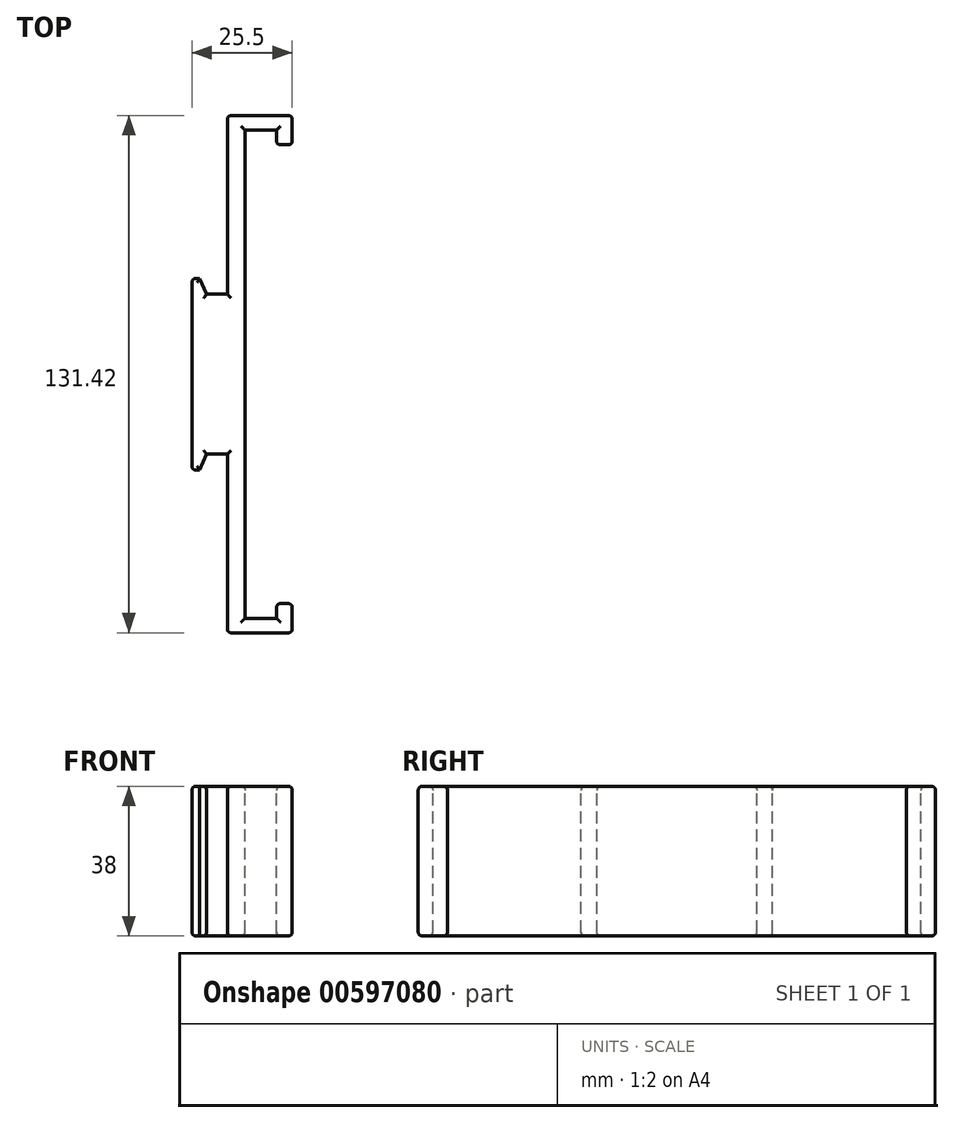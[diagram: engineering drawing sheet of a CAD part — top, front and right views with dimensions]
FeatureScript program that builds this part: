
annotation { "Feature Type Name" : "Feature", "Feature Type Description" : "" }
export const myFeature = defineFeature(function(context is Context, id is Id, definition is map)
    precondition{}
    {
        {
            var Q0;
            Q0=qCreatedBy(makeId("Top.planeOp"),FACE);
            var sketch = newSketch(context, id + "F0", { "sketchPlane" : qUnion([Q0])});
            skLineSegment(sketch, "E0", {"start": v(0, 0) * mm, "end": v(0, 65.71) * mm});
            skLineSegment(sketch, "E1", {"start": v(0, 65.71) * mm, "end": v(12.5, 65.71) * mm});
            skLineSegment(sketch, "E2", {"start": v(12.5, 62) * mm, "end": v(12.5, 58.29) * mm});
            skLineSegment(sketch, "E3", {"start": v(16.5, 58.29) * mm, "end": v(12.5, 58.29) * mm});
            skLineSegment(sketch, "E4", {"start": v(16.5, 58.29) * mm, "end": v(16.5, 62) * mm});
            skPoint(sketch, "E4.endSnap0", {"position": v(12.5, 62) * mm});
            skLineSegment(sketch, "E5", {"start": v(12.5, 62) * mm, "end": v(4.5, 62) * mm});
            skLineSegment(sketch, "E6", {"start": v(4.5, 62) * mm, "end": v(4.5, 0) * mm});
            skLineSegment(sketch, "E7", {"start": v(0, 20.33) * mm, "end": v(-5.29, 20.33) * mm});
            skLineSegment(sketch, "E8", {"start": v(-7, 24.33) * mm, "end": v(-9, 24.33) * mm});
            skLineSegment(sketch, "E9", {"start": v(-9, 24.33) * mm, "end": v(-9, 0) * mm});
            skLineSegment(sketch, "E10", {"start": v(16.5, 62) * mm, "end": v(16.5, 65.71) * mm});
            skLineSegment(sketch, "E11", {"start": v(16.5, 65.71) * mm, "end": v(12.5, 65.71) * mm});
            skLineSegment(sketch, "E12", {"start": v(0, 0) * mm, "end": v(27.16, 0) * mm, "construction": true});
            skLineSegment(sketch, "E13.MirrorCS", {"start": v(0, 0) * mm, "end": v(0, -65.71) * mm});
            skLineSegment(sketch, "E14.MirrorCS", {"start": v(4.5, -62) * mm, "end": v(4.5, 0) * mm});
            skLineSegment(sketch, "E15.MirrorCS", {"start": v(12.5, -62) * mm, "end": v(4.5, -62) * mm});
            skLineSegment(sketch, "E16.MirrorCS", {"start": v(0, -65.71) * mm, "end": v(12.5, -65.71) * mm});
            skLineSegment(sketch, "E17.MirrorCS", {"start": v(12.5, -62) * mm, "end": v(12.5, -58.29) * mm});
            skLineSegment(sketch, "E18.MirrorCS", {"start": v(16.5, -62) * mm, "end": v(16.5, -65.71) * mm});
            skLineSegment(sketch, "E19.MirrorCS", {"start": v(16.5, -58.29) * mm, "end": v(16.5, -62) * mm});
            skLineSegment(sketch, "E20.MirrorCS", {"start": v(16.5, -65.71) * mm, "end": v(12.5, -65.71) * mm});
            skLineSegment(sketch, "E21.MirrorCS", {"start": v(16.5, -58.29) * mm, "end": v(12.5, -58.29) * mm});
            skLineSegment(sketch, "E22.MirrorCS", {"start": v(0, -20.33) * mm, "end": v(-5.29, -20.33) * mm});
            skLineSegment(sketch, "E23.MirrorCS", {"start": v(-7, -24.33) * mm, "end": v(-9, -24.33) * mm});
            skLineSegment(sketch, "E24.MirrorCS", {"start": v(-9, -24.33) * mm, "end": v(-9, 0) * mm});
            skLineSegment(sketch, "E25", {"start": v(-7, 24.33) * mm, "end": v(-5.29, 20.33) * mm});
            skPoint(sketch, "E26.orphan", {"position": v(-7, 20.33) * mm});
            skLineSegment(sketch, "E27.MirrorCS", {"start": v(-7, -24.33) * mm, "end": v(-5.29, -20.33) * mm});
            skPoint(sketch, "E28.orphan", {"position": v(-7, -20.33) * mm});
            skPoint(sketch, "E29.MirrorCS.end.orphan", {"position": v(-7, -24.33) * mm});
            skSolve(sketch);
        }
        {
            var Q0;
            {var subQ4=sQuery(id+"F0.wireOp",EDGE,"E1");Q0=makeQuery(id+"F0.imprint","IMPRINT",FACE,{"disambiguationData":[TD([[makeQuery(id+"F0.imprint","IMPRINT",EDGE,{"derivedFrom":subQ4}),-1.0]])]});}
            var Q1;
            {var subQ0=sQuery(id+"F0.wireOp",EDGE,"E7");Q1=makeQuery(id+"F0.imprint","IMPRINT",FACE,{"disambiguationData":[TD([[makeQuery(id+"F0.imprint","IMPRINT",EDGE,{"derivedFrom":subQ0}),1.0]])]});}
            extrude(context, id + "F1", {"entities" : qUnion([Q0, Q1]), "oppositeDirection" : true, "depth" : 4 * mm, "offsetDistance" : 25 * mm});
        }
        {
            var Q0;
            Q0 = qSketchRegion(id + "F0", true);
            extrude(context, id + "F2", {"entities" : qUnion([Q0]), "operationType" : NewBodyOperationType.ADD, "oppositeDirection" : true, "depth" : 38 * mm, "offsetDistance" : 25 * mm});
        }
        {
            var Q0;
            Q0=makeQuery(id+"F1.opExtrude","CAP_FACE",FACE,{"disambiguationData":[OSD([sQuery(id+"F0.wireOp",EDGE,"E0"),sQuery(id+"F0.wireOp",EDGE,"E1"),sQuery(id+"F0.wireOp",EDGE,"E2"),sQuery(id+"F0.wireOp",EDGE,"E3"),sQuery(id+"F0.wireOp",EDGE,"E4"),sQuery(id+"F0.wireOp",EDGE,"E5"),sQuery(id+"F0.wireOp",EDGE,"E6"),sQuery(id+"F0.wireOp",EDGE,"E7"),sQuery(id+"F0.wireOp",EDGE,"E8"),sQuery(id+"F0.wireOp",EDGE,"E9"),sQuery(id+"F0.wireOp",EDGE,"E10"),sQuery(id+"F0.wireOp",EDGE,"E11"),sQuery(id+"F0.wireOp",EDGE,"E13.MirrorCS"),sQuery(id+"F0.wireOp",EDGE,"E14.MirrorCS"),sQuery(id+"F0.wireOp",EDGE,"E15.MirrorCS"),sQuery(id+"F0.wireOp",EDGE,"E17.MirrorCS"),sQuery(id+"F0.wireOp",EDGE,"E18.MirrorCS"),sQuery(id+"F0.wireOp",EDGE,"E19.MirrorCS"),sQuery(id+"F0.wireOp",EDGE,"E20.MirrorCS"),sQuery(id+"F0.wireOp",EDGE,"E16.MirrorCS"),sQuery(id+"F0.wireOp",EDGE,"E21.MirrorCS"),sQuery(id+"F0.wireOp",EDGE,"E22.MirrorCS"),sQuery(id+"F0.wireOp",EDGE,"E23.MirrorCS"),sQuery(id+"F0.wireOp",EDGE,"E24.MirrorCS"),sQuery(id+"F0.wireOp",EDGE,"E25"),sQuery(id+"F0.wireOp",EDGE,"E27.MirrorCS")])],"isStart":true});
            var Q1;
            Q1=makeQuery(id+"F2.opExtrude","CAP_FACE",FACE,{"disambiguationData":[OSD([sQuery(id+"F0.wireOp",EDGE,"E0"),sQuery(id+"F0.wireOp",EDGE,"E1"),sQuery(id+"F0.wireOp",EDGE,"E2"),sQuery(id+"F0.wireOp",EDGE,"E3"),sQuery(id+"F0.wireOp",EDGE,"E4"),sQuery(id+"F0.wireOp",EDGE,"E5"),sQuery(id+"F0.wireOp",EDGE,"E6"),sQuery(id+"F0.wireOp",EDGE,"E7"),sQuery(id+"F0.wireOp",EDGE,"E8"),sQuery(id+"F0.wireOp",EDGE,"E9"),sQuery(id+"F0.wireOp",EDGE,"E10"),sQuery(id+"F0.wireOp",EDGE,"E11"),sQuery(id+"F0.wireOp",EDGE,"E13.MirrorCS"),sQuery(id+"F0.wireOp",EDGE,"E14.MirrorCS"),sQuery(id+"F0.wireOp",EDGE,"E15.MirrorCS"),sQuery(id+"F0.wireOp",EDGE,"E17.MirrorCS"),sQuery(id+"F0.wireOp",EDGE,"E18.MirrorCS"),sQuery(id+"F0.wireOp",EDGE,"E19.MirrorCS"),sQuery(id+"F0.wireOp",EDGE,"E20.MirrorCS"),sQuery(id+"F0.wireOp",EDGE,"E16.MirrorCS"),sQuery(id+"F0.wireOp",EDGE,"E21.MirrorCS"),sQuery(id+"F0.wireOp",EDGE,"E22.MirrorCS"),sQuery(id+"F0.wireOp",EDGE,"E23.MirrorCS"),sQuery(id+"F0.wireOp",EDGE,"E24.MirrorCS"),sQuery(id+"F0.wireOp",EDGE,"E25"),sQuery(id+"F0.wireOp",EDGE,"E27.MirrorCS")])],"isStart":false});
            var Q2;
            {var subQ0=sQuery(id+"F0.wireOp",EDGE,"E21.MirrorCS");Q2=makeQuery(id+"F2.boolean.opBoolean","MERGE",FACE,{"derivedFrom":[makeQuery(id+"F1.opExtrude","SWEPT_FACE",FACE,{"disambiguationData":[OSD([subQ0])]}),makeQuery(id+"F2.opExtrude","SWEPT_FACE",FACE,{"disambiguationData":[OSD([subQ0])]})]});}
            var Q3;
            {var subQ0=sQuery(id+"F0.wireOp",EDGE,"E3");Q3=makeQuery(id+"F2.boolean.opBoolean","MERGE",FACE,{"derivedFrom":[makeQuery(id+"F1.opExtrude","SWEPT_FACE",FACE,{"disambiguationData":[OSD([subQ0])]}),makeQuery(id+"F2.opExtrude","SWEPT_FACE",FACE,{"disambiguationData":[OSD([subQ0])]})]});}
            var Q4;
            {var subQ0=sQuery(id+"F0.wireOp",EDGE,"E24.MirrorCS");var subQ1=sQuery(id+"F0.wireOp",EDGE,"E9");Q4=makeQuery(id+"F2.boolean.opBoolean","MERGE",FACE,{"derivedFrom":[makeQuery(id+"F1.opExtrude","SWEPT_FACE",FACE,{"disambiguationData":[OSD([subQ1,subQ0])]}),makeQuery(id+"F2.opExtrude","SWEPT_FACE",FACE,{"disambiguationData":[OSD([subQ1,subQ0])]})]});}
            var Q5;
            {var subQ0=sQuery(id+"F0.wireOp",EDGE,"E11");var subQ1=sQuery(id+"F0.wireOp",EDGE,"E1");Q5=makeQuery(id+"F2.boolean.opBoolean","MERGE",FACE,{"derivedFrom":[makeQuery(id+"F1.opExtrude","SWEPT_FACE",FACE,{"disambiguationData":[OSD([subQ1,subQ0])]}),makeQuery(id+"F2.opExtrude","SWEPT_FACE",FACE,{"disambiguationData":[OSD([subQ1,subQ0])]})]});}
            var Q6;
            {var subQ0=sQuery(id+"F0.wireOp",EDGE,"E16.MirrorCS");var subQ1=sQuery(id+"F0.wireOp",EDGE,"E20.MirrorCS");Q6=makeQuery(id+"F2.boolean.opBoolean","MERGE",FACE,{"derivedFrom":[makeQuery(id+"F1.opExtrude","SWEPT_FACE",FACE,{"disambiguationData":[OSD([subQ1,subQ0])]}),makeQuery(id+"F2.opExtrude","SWEPT_FACE",FACE,{"disambiguationData":[OSD([subQ1,subQ0])]})]});}
            fillet(context, id + "F3", {"entities" : qUnion([Q0, Q1, Q2, Q3, Q4, Q5, Q6]), "radius" : 1 * mm, "tangentPropagation" : true, "allowEdgeOverflow" : false});
        }
    });
